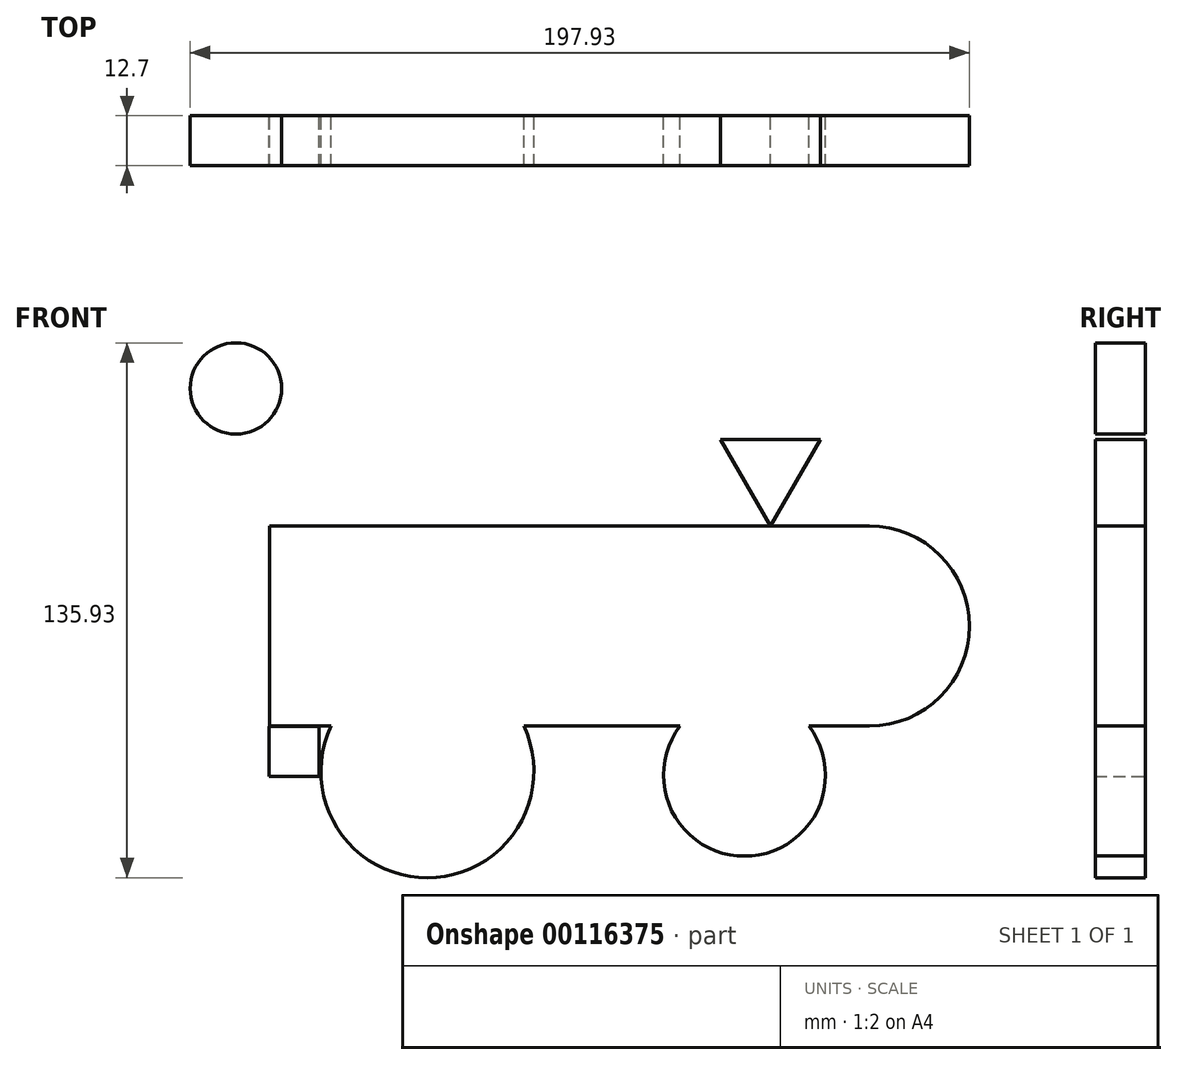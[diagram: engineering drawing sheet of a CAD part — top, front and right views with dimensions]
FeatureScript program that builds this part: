
annotation { "Feature Type Name" : "Feature", "Feature Type Description" : "" }
export const myFeature = defineFeature(function(context is Context, id is Id, definition is map)
    precondition{}
    {
        {
            var Q0;
            Q0=qCreatedBy(makeId("Front.planeOp"),FACE);
            var sketch = newSketch(context, id + "F0", { "sketchPlane" : qUnion([Q0])});
            skCircle(sketch, "E0", {"center": v(-59.95, 58.15) * mm, "radius": 11.6 * mm});
            skSolve(sketch);
        }
        {
            var Q0;
            Q0=qCreatedBy(makeId("Front.planeOp"),FACE);
            var sketch = newSketch(context, id + "F1", { "sketchPlane" : qUnion([Q0])});
            skLineSegment(sketch, "E1.bottom", {"start": v(-51.43, 23.17) * mm, "end": v(100.97, 23.17) * mm});
            skLineSegment(sketch, "E1.top", {"start": v(-51.43, -27.63) * mm, "end": v(100.97, -27.63) * mm});
            skLineSegment(sketch, "E1.left", {"start": v(-51.43, 23.17) * mm, "end": v(-51.43, -27.63) * mm});
            skLineSegment(sketch, "E1.right", {"start": v(100.97, 23.17) * mm, "end": v(100.97, -27.63) * mm});
            skArc(sketch, "E2", {"start": v(126.27, 0) * mm, "mid": v(118.12, 16.5) * mm, "end": v(100.97, 23.17) * mm});
            skArc(sketch, "E3", {"start": v(100.97, -27.63) * mm, "mid": v(119.7, -19.38) * mm, "end": v(126.27, 0) * mm});
            skCircle(sketch, "E4", {"center": v(69.26, -40.08) * mm, "radius": 20.58 * mm});
            skLineSegment(sketch, "E5.bottom", {"start": v(-51.47, -27.72) * mm, "end": v(-38.77, -27.72) * mm});
            skLineSegment(sketch, "E5.top", {"start": v(-51.47, -40.42) * mm, "end": v(-38.77, -40.42) * mm});
            skLineSegment(sketch, "E5.left", {"start": v(-51.47, -27.72) * mm, "end": v(-51.47, -40.42) * mm});
            skLineSegment(sketch, "E5.right", {"start": v(-38.77, -27.72) * mm, "end": v(-38.77, -40.42) * mm});
            skCircle(sketch, "E6", {"center": v(-11.3, -39.11) * mm, "radius": 27.06 * mm});
            skLineSegment(sketch, "E7.0", {"start": v(75.83, 23.17) * mm, "end": v(63.19, 45.2) * mm});
            skLineSegment(sketch, "E7.1", {"start": v(63.19, 45.2) * mm, "end": v(88.59, 45.13) * mm});
            skLineSegment(sketch, "E7.2", {"start": v(88.59, 45.13) * mm, "end": v(75.83, 23.17) * mm});
            skPoint(sketch, "E7.0.midPoint", {"position": v(69.5, 34.19) * mm});
            skLineSegment(sketch, "E8.bottom", {"start": v(-51.43, 23.17) * mm, "end": v(-0.63, 23.17) * mm});
            skLineSegment(sketch, "E8.top", {"start": v(-51.43, 48.57) * mm, "end": v(-0.63, 48.57) * mm});
            skLineSegment(sketch, "E8.left", {"start": v(-51.43, 23.17) * mm, "end": v(-51.43, 48.57) * mm});
            skLineSegment(sketch, "E8.right", {"start": v(-0.63, 23.17) * mm, "end": v(-0.63, 48.57) * mm});
            skPoint(sketch, "E9.startSnap0", {"position": v(75.89, 45.17) * mm});
            skLineSegment(sketch, "E10", {"start": v(100.97, -27.63) * mm, "end": v(69.26, -40.08) * mm, "construction": true});
            skLineSegment(sketch, "E11", {"start": v(69.26, -40.08) * mm, "end": v(69.26, -27.63) * mm, "construction": true});
            skLineSegment(sketch, "E12", {"start": v(-11.3, -39.11) * mm, "end": v(-38.77, -27.72) * mm, "construction": true});
            skLineSegment(sketch, "E13", {"start": v(-11.3, -39.11) * mm, "end": v(-11.3, -27.63) * mm});
            skSolve(sketch);
        }
        {
            var Q0;
            Q0=makeQuery(id+"F1.imprint","IMPRINT",FACE,{"disambiguationData":[TD([[makeQuery(id+"F1.imprint","IMPRINT",EDGE,{"derivedFrom":sQuery(id+"F1.wireOp",EDGE,"E1.right")}),1.0]])]});
            var Q1;
            {var subQ0=sQuery(id+"F1.wireOp",EDGE,"E4");var subQ1=sQuery(id+"F1.wireOp",EDGE,"E1.top");var subQ2=makeQuery(id+"F1.imprint","INTERSECT",VERTEX,{"disambiguationData":[OD(0.0)],"derivedFrom":[subQ1,subQ0]});Q1=makeQuery(id+"F1.imprint","IMPRINT",FACE,{"disambiguationData":[TD([[makeQuery(id+"F1.imprint","IMPRINT",EDGE,{"disambiguationData":[TD([[subQ2,-1.0]])],"derivedFrom":subQ1}),1.0]])]});}
            var Q2;
            Q2=makeQuery(id+"F1.imprint","IMPRINT",FACE,{"disambiguationData":[TD([[makeQuery(id+"F1.imprint","IMPRINT",EDGE,{"derivedFrom":sQuery(id+"F1.wireOp",EDGE,"E5.bottom")}),-1.0]])]});
            var Q3;
            {var subQ0=sQuery(id+"F1.wireOp",EDGE,"E1.left");Q3=makeQuery(id+"F1.imprint","IMPRINT",FACE,{"disambiguationData":[TD([[makeQuery(id+"F1.imprint","IMPRINT",EDGE,{"derivedFrom":subQ0}),1.0]])]});}
            var Q4;
            Q4=makeQuery(id+"F1.imprint","IMPRINT",FACE,{"disambiguationData":[TD([[makeQuery(id+"F1.imprint","IMPRINT",EDGE,{"derivedFrom":sQuery(id+"F1.wireOp",EDGE,"E8.bottom")}),1.0]])]});
            var Q5;
            {var subQ0=sQuery(id+"F1.wireOp",EDGE,"E1.top");var subQ1=makeQuery(id+"F1.imprint","IMPRINT",VERTEX,{"derivedFrom":subQ0});Q5=makeQuery(id+"F1.imprint","IMPRINT",FACE,{"disambiguationData":[TD([[makeQuery(id+"F1.imprint","IMPRINT",EDGE,{"disambiguationData":[TD([[subQ1,1.0]])],"derivedFrom":subQ0}),1.0]])]});}
            var Q6;
            Q6=makeQuery(id+"F1.imprint","IMPRINT",FACE,{"disambiguationData":[TD([[makeQuery(id+"F1.imprint","IMPRINT",EDGE,{"derivedFrom":sQuery(id+"F1.wireOp",EDGE,"E7.0")}),-1.0]])]});
            var Q7;
            {var subQ0=sQuery(id+"F1.wireOp",EDGE,"E1.top");var subQ1=makeQuery(id+"F1.imprint","IMPRINT",VERTEX,{"derivedFrom":subQ0});Q7=makeQuery(id+"F1.imprint","IMPRINT",FACE,{"disambiguationData":[TD([[makeQuery(id+"F1.imprint","IMPRINT",EDGE,{"disambiguationData":[TD([[subQ1,1.0]])],"derivedFrom":subQ0}),-1.0]])]});}
            var Q8;
            Q8=makeQuery(id+"F0.imprint","IMPRINT",FACE,{"disambiguationData":[TD([[makeQuery(id+"F0.imprint","IMPRINT",EDGE,{"derivedFrom":sQuery(id+"F0.wireOp",EDGE,"E0")}),1.0]])]});
            var Q9;
            {var subQ0=sQuery(id+"F1.wireOp",EDGE,"E4");var subQ1=sQuery(id+"F1.wireOp",EDGE,"E1.top");var subQ2=makeQuery(id+"F1.imprint","INTERSECT",VERTEX,{"disambiguationData":[OD(0.0)],"derivedFrom":[subQ1,subQ0]});Q9=makeQuery(id+"F1.imprint","IMPRINT",FACE,{"disambiguationData":[TD([[makeQuery(id+"F1.imprint","IMPRINT",EDGE,{"disambiguationData":[TD([[subQ2,-1.0]])],"derivedFrom":subQ1}),-1.0]])]});}
            extrude(context, id + "F2", {"entities" : qUnion([Q0, Q1, Q2, Q3, Q4, Q5, Q6, Q7, Q8, Q9]), "depth" : 12.7 * mm});
        }
    });
